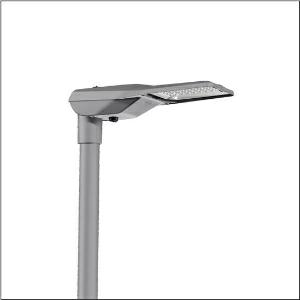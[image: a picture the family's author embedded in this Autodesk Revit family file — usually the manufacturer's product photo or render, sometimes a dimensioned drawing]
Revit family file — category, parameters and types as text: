
# Revit family: streetlight_sl_21_iq_mini___stw1_0a_5xe2e31y08gb_7efe
name_source: partatom
category: Lighting Fixtures
units: mm (PartAtom-declared; Revit-internal decimal feet)

## family parameters
Cut with Voids When Loaded = No
Host = Face
Light Source = No
Part Type = Normal
Room Calculation Point = No
Round Connector Dimension = Use Diameter
Shared = No

## types (1)
- --- (1 x LED, 5990 lm, 39.8 W, 3000K)
    Apparent Load = 40 VA
    CIE Flux Codes = 38 75 98 100 100
    Color Rendering = 70
    Color Temperature = 3000K
    Default Elevation = 1800 mm
    Description = Streetlight SL 21 iQ mini, mast luminaire, primary light control with lens, of PMMA, primary optical cover: cover, of toughened safety glass, transparent, light distribution: STW1.0a, light emission: direct distribution, primary light characteristic: asymmetric, installation type: post-top, side-entry, LED, High Power LED, rated luminous flux: 5.990lm, luminous efficacy: 151lm/W, light colour: 730, colour temperature: 3000K, control gear: iQ-Street Remote, D4i with power reduction, control: pre-setting: logarithmic dimming characteristic, Street-Remote, Auto-Match, Temp-Guard, Lumen-Switch, Night-Set, Smart-Wire, Light-Fading, Desk-Remote (wireless, voltage-free reading and setting of iQ features in the workshop via application-optimized NFC function/RFID function), optimised constant luminous flux control (CLO 2.0), mains connection: 220..240V, AC, 50/60Hz, start of lifetime: 40W, end of service life: 41W, reduction: 18W, luminaire housing, of diecast aluminium, powder-coated, SITECO metallic grey (DB 702S), corrosivity category C5 high according to DIN EN ISO 12944, please order mast flange separately, inclination adjustable: 0°, 5°, 10°, 15°, sealing non-destructively replaceable, multi-level sealing system, length: 628mm, width: 235mm, height: 110mm, mast flange for spigot size: 42mm (side-entry): 5XC10008XM4, 60/48mm (side-entry/post-top): 5XC10108XM2, 76/60mm (side-entry/post-top): 5XC10108XM1, mounting height: 4..8m, Smart Interface below and above, protection rating (complete): IP66, insulation class (complete): insulation class II (safety insulation), certification: CE, ENEC, ENEC+, VDE, impact resistance: IK10, permissible operating ambient temperature for outdoor applications: -40..+50°C, standard-compliant lighting for roads and squares, packaging unit: 1 piece

Light Distribution: STW1.0a
    Height = 110 mm
    Lamp = 1 x LED
    Lamp Light Flux = 5990 lm
    Lamp Power = 39.8 W
    Lamp count = 1
    Length = 625 mm
    Luminous efficacy = 151 lm/W
    Manufacturer = Siteco
    ModVariant = No
    Model = 5XE2E31Y08GB
    Mounting Place = Pole
    Mounting Type = Pole top
    Number of Poles = 1
    OnlyDefault = Yes
    Power Factor = 1
    Product Name = Streetlight SL 21 iQ mini | STW1.0a
    Product group = mast luminaire | pylon top
    ProductGroupID = 6100
    Protection Class = Protection class II
    Protection Degree = IP 66
    RLX_Detail_Level = 1
    RLX_Emergency_Light_Flux = 0 lm
    RLX_Emergency_Type = 0
    RLX_Emergency_Type_DB = No
    RlxData = <blob elided: 92693 chars, md5=073d114a>
    Socket = socket
    Standby Power = 0 W
    System Light Flux = 5990 lm
    System Power = 40 W
    Type Comments = factory setting: luminous flux: 100 % | dim-lin: 254 | 800 mA
    Type Image = l_1003514.jpg
    URL = http://relux.com
    VarID = @adj_116017
    Voltage = 0 V
    Weight = 0.00 kg
    Width = 234 mm

## geometry (parser evidence)
native form markers: Blend x4, Sweep x12
no freeform markers — native parametric forms only
